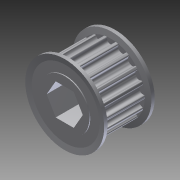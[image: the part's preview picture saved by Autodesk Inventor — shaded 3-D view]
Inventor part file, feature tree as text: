
AUTODESK INVENTOR PART (.ipt)
format: ipt  version: 2014 (Build 180170000, 170)  size: 654,848 bytes
history: native  units: in
note: dims shown in document units (in); Inventor stores cm internally (conversion verified against a paired STEP export)
features: mirror x1, other x1, imported_body x1
ambient origin geometry x8: Origin, YZ Plane, XZ Plane, XY Plane, X Axis, Y Axis, Z Axis, Center Point
bodies: Body1 (feature_tree)
feature tree (3):
  mirror  "Mirror1"
  other  "217-3226-STEP1"
  imported_body  "Base1"
